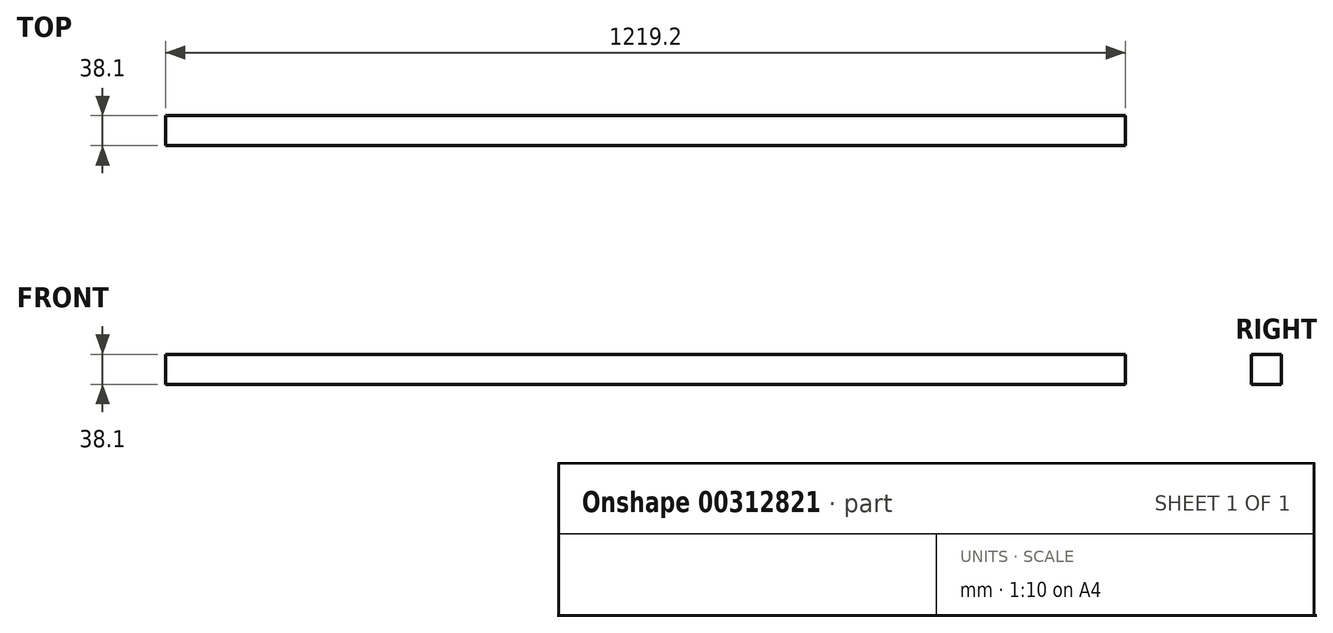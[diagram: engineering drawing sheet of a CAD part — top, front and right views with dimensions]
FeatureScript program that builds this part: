
annotation { "Feature Type Name" : "Feature", "Feature Type Description" : "" }
export const myFeature = defineFeature(function(context is Context, id is Id, definition is map)
    precondition{}
    {
        {
            var Q0;
            Q0=qCreatedBy(makeId("Front.planeOp"),FACE);
            var sketch = newSketch(context, id + "F0", { "sketchPlane" : qUnion([Q0])});
            skLineSegment(sketch, "E0.bottom", {"start": v(-259.47, 0) * mm, "end": v(959.73, 0) * mm});
            skLineSegment(sketch, "E0.top", {"start": v(-259.47, -38.1) * mm, "end": v(959.73, -38.1) * mm});
            skLineSegment(sketch, "E0.left", {"start": v(-259.47, 0) * mm, "end": v(-259.47, -38.1) * mm});
            skLineSegment(sketch, "E0.right", {"start": v(959.73, 0) * mm, "end": v(959.73, -38.1) * mm});
            skSolve(sketch);
        }
        {
            var Q0;
            Q0 = qSketchRegion(id + "F0", true);
            extrude(context, id + "F1", {"entities" : qUnion([Q0]), "depth" : 38.1 * mm});
        }
    });
